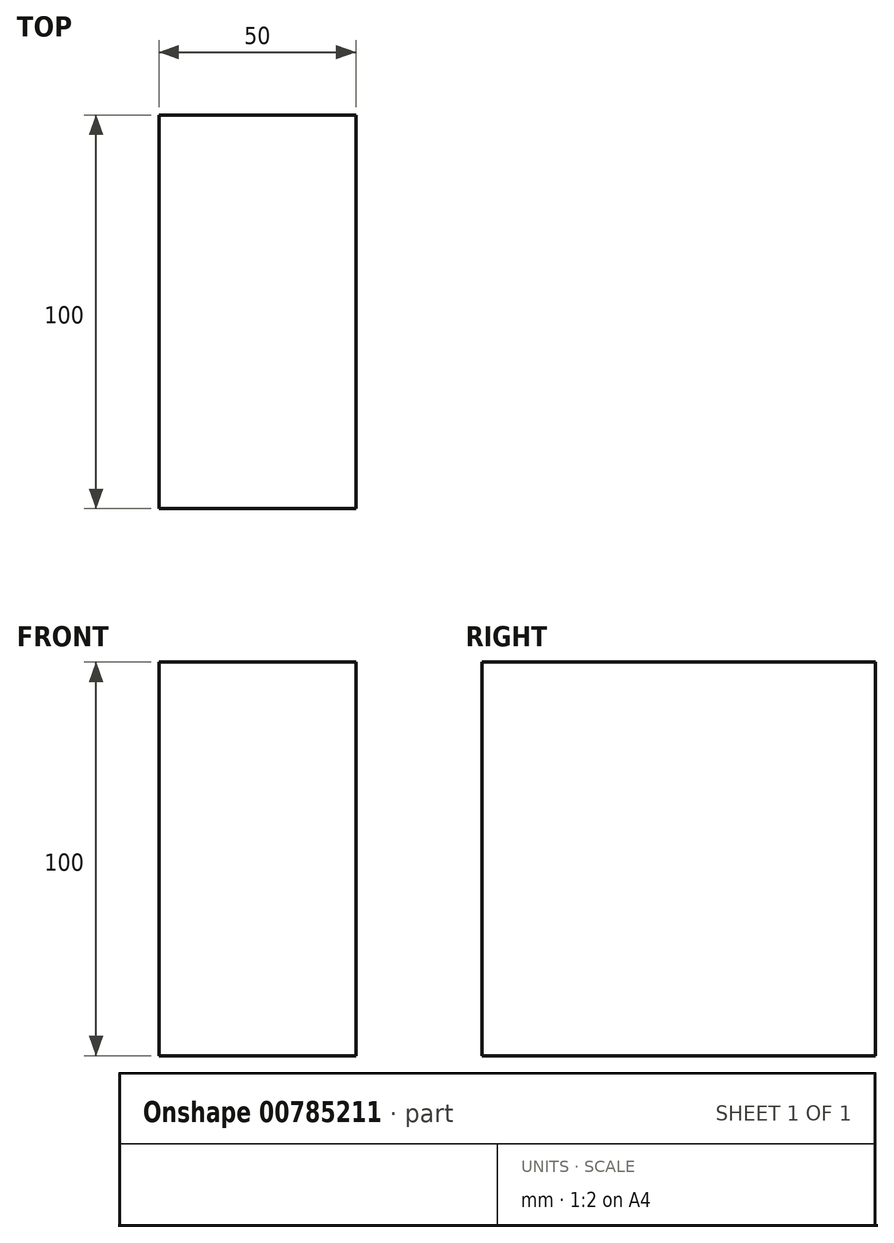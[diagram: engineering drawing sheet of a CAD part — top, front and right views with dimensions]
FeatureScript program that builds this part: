
annotation { "Feature Type Name" : "Feature", "Feature Type Description" : "" }
export const myFeature = defineFeature(function(context is Context, id is Id, definition is map)
    precondition{}
    {
        {
            var Q0;
            Q0=qCreatedBy(makeId("Front.planeOp"),FACE);
            var sketch = newSketch(context, id + "F0", { "sketchPlane" : qUnion([Q0])});
            skLineSegment(sketch, "E0.top", {"start": v(0, 100) * mm, "end": v(50, 100) * mm});
            skLineSegment(sketch, "E0.left", {"start": v(0, 0) * mm, "end": v(0, 100) * mm});
            skLineSegment(sketch, "E0.right", {"start": v(50, 0) * mm, "end": v(50, 100) * mm});
            skLineSegment(sketch, "E1", {"start": v(0, 0) * mm, "end": v(50, 0) * mm});
            skSolve(sketch);
        }
        {
            var Q0;
            Q0=makeQuery(id+"F0.imprint","IMPRINT",FACE,{"disambiguationData":[TD([[makeQuery(id+"F0.imprint","IMPRINT",EDGE,{"derivedFrom":sQuery(id+"F0.wireOp",EDGE,"E0.top")}),-1.0]])]});
            extrude(context, id + "F1", {"entities" : qUnion([Q0]), "depth" : 100 * mm, "offsetDistance" : 25 * mm});
        }
    });
